# Revit family: Water_Dispenser_Filtered-Elkay-DSBS130UVPC
name_source: partatom
category: Plumbing Fixtures
units: mm (PartAtom-declared; Revit-internal decimal feet)

## family parameters
Always vertical = Yes
Cut with Voids When Loaded = No
Maintain Annotation Orientation = No
OmniClass Number = 23.45.00.00
OmniClass Title = Sanitary, Laundry, and Cleaning Equipment
Part Type = Normal
Room Calculation Point = No
Round Connector Dimension = Use Diameter
Shared = No
Work Plane-Based = No

## types (1)
- DSBS130UVPC (Water Dispenser Filtered Refrigerated 1.5 GPH Stainless )
    Approx. Shipping Weight (lbs) = 66
    Assembly Code = D2010800
    Buttons Pad = Glass
    Buttons dia = 13/16"
    CW Connection = Yes
    Chilling Capacity(GPH) = 1.5 GPH
    Current = 0 A
    Default Elevation = 0"
    Description = Water Dispenser Filtered Refrigerated 1.5 GPH Stainless Steel
    Dimensions (L x W x H) = "19 3/16 inch x 10 1/4 inch x 16 7/16 inch"
    Footings dia = 9/16"
    Front Panel = Finish-Elkay-Midnight Black
    HW Connection = Yes
    Height = 16 1/2"
    Inlet Connection Size (inch) = 1/4"
    Length = 19 3/16"
    Main Material = Finish-Elkay-Steel
    Manufacturer = Elkay Manufacturer Company
    Manufacturer Brand = Elkay (by Zurn Elkay Water Solutions)
    Model = DSBS130UVPC
    Number of Poles = 1
    Power Factor = 1
    Product Documentation Link = https://www.elkayfiles.com
    Product Installation Sheet URL = https://www.elkayfiles.com
    Product Page URL = https://www.elkay.com
    Product Weight (lbs) = 52
    Product data URL = https://www.bimobject.com
    Repair Parts URL = https://www.elkayfiles.com
    URL = https://www.elkay.com
    Vent Connection = Yes
    Voltage = 115 V
    Waste Connection = Yes

## geometry (parser evidence)
native form markers: Sweep x2
no freeform markers — native parametric forms only
